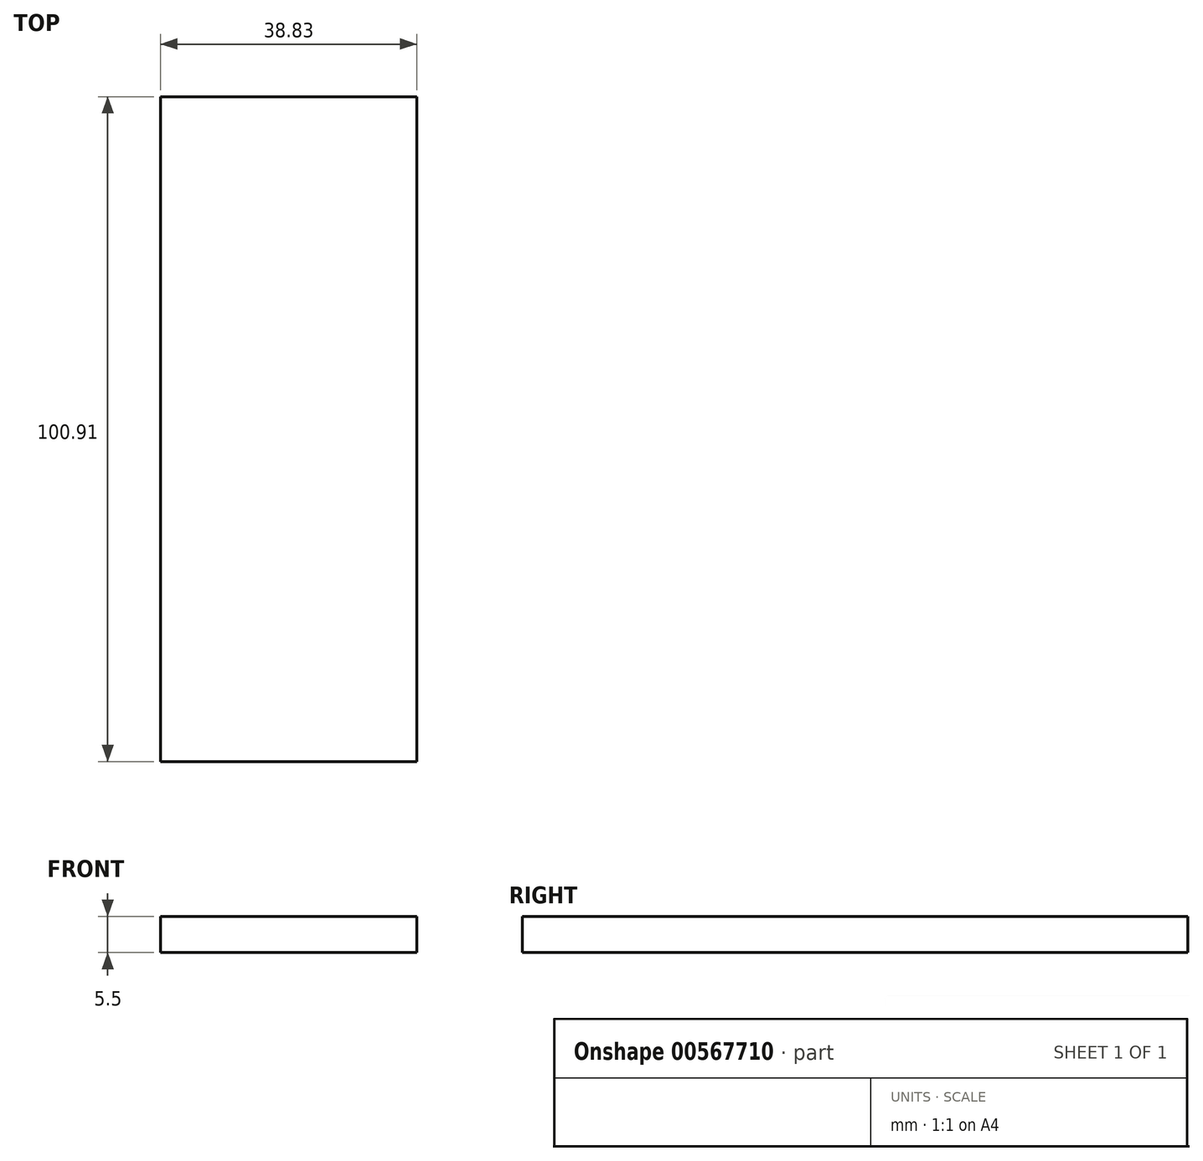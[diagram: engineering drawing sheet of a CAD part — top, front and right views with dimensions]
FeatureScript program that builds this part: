
annotation { "Feature Type Name" : "Feature", "Feature Type Description" : "" }
export const myFeature = defineFeature(function(context is Context, id is Id, definition is map)
    precondition{}
    {
        {
            var Q0;
            Q0=qCreatedBy(makeId("Top.planeOp"),FACE);
            cPlane(context, id + "F0", {"entities" : qUnion([Q0]), "cplaneType" : CPlaneType.OFFSET, "offset" : 65 * mm, "oppositeDirection" : true, "width" : 150 * mm, "height" : 150 * mm});
        }
        {
            var Q0;
            Q0=qCreatedBy(id+"F0.planeOp",FACE);
            var sketch = newSketch(context, id + "F1", { "sketchPlane" : qUnion([Q0])});
            skLineSegment(sketch, "E0.bottom", {"start": v(-51.78, 6.64) * mm, "end": v(-12.95, 6.64) * mm});
            skLineSegment(sketch, "E0.top", {"start": v(-51.78, 107.55) * mm, "end": v(-12.95, 107.55) * mm});
            skLineSegment(sketch, "E0.left", {"start": v(-51.78, 6.64) * mm, "end": v(-51.78, 107.55) * mm});
            skLineSegment(sketch, "E0.right", {"start": v(-12.95, 6.64) * mm, "end": v(-12.95, 107.55) * mm});
            skSolve(sketch);
        }
        {
            var Q0;
            Q0=makeQuery(id+"F1.imprint","IMPRINT",FACE,{"disambiguationData":[TD([[makeQuery(id+"F1.imprint","IMPRINT",EDGE,{"derivedFrom":sQuery(id+"F1.wireOp",EDGE,"E0.bottom")}),1.0]])]});
            extrude(context, id + "F2", {"entities" : qUnion([Q0]), "depth" : 5.5 * mm, "offsetDistance" : 25 * mm});
        }
    });
